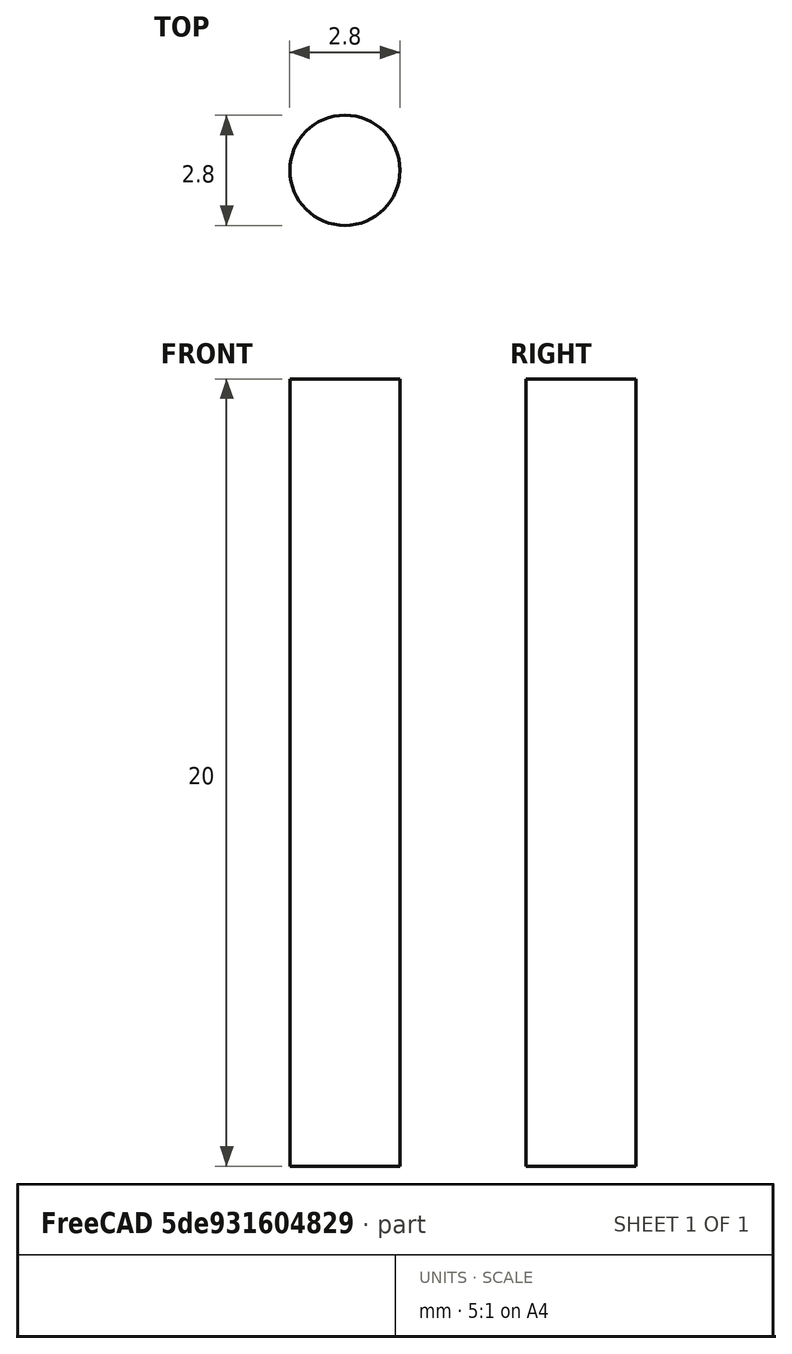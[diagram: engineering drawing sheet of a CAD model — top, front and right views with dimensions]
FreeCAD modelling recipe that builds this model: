
FCSTD DOCUMENT  (FreeCAD 1.0R38641 +468 (Git))
Label: Pin
License: All rights reserved
LicenseURL: https://en.wikipedia.org/wiki/All_rights_reserved
objects: Sketcher::SketchObject×1, PartDesign::Pad×1, PartDesign::Body×1
note: 6 computed .brp shape members not serialized (recipe doc carries the construction recipe); baked Part::Feature solids carry a one-line shape summary decoded from their .brp

FEATURE [Sketcher::SketchObject] Sketch206  label="pin"
  ArcFitTolerance = 1e-06
  AttachmentSupport = -> [XY_Plane022]
  FullyConstrained = false
  MakeInternals = false
  MapMode = 5
  sketch-geometry (1):
    g0: Circle CenterX=4.17307 CenterY=2.45272 CenterZ=0 NormalX=0 NormalY=0 NormalZ=1 AngleXU=0 Radius=1.4
  constraints (1):
    c: Diameter(g0) = 2.8
FEATURE [PartDesign::Pad] Pad102
  Direction = (0,0,1)
  Length = 20
  Length2 = 10
  Profile = -> Sketch206
  ReferenceAxis = -> Sketch206 [N_Axis]
  Refine = true
  Suppressed = false
  Type = 0
FEATURE [PartDesign::Body] Body022  label="Pin"
  AllowCompound = false
  Group = -> [Sketch206,Pad102]
  Origin = -> Origin022
  Tip = -> Pad102
